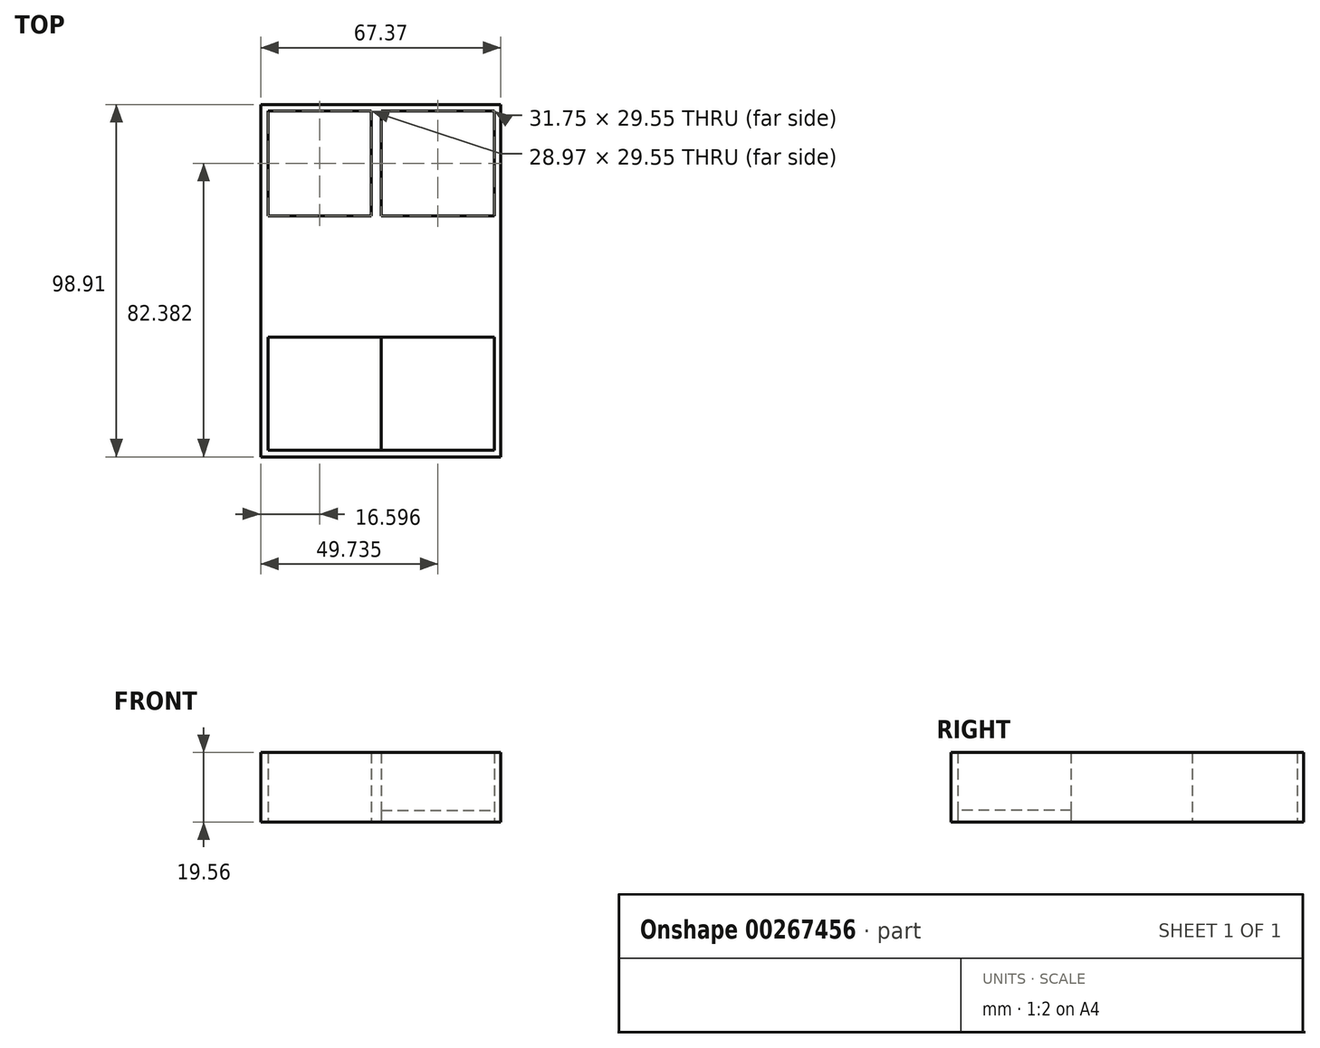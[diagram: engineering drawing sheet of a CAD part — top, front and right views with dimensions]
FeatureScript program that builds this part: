
annotation { "Feature Type Name" : "Feature", "Feature Type Description" : "" }
export const myFeature = defineFeature(function(context is Context, id is Id, definition is map)
    precondition{}
    {
        {
            var Q0;
            Q0=qCreatedBy(makeId("Top.planeOp"),FACE);
            var sketch = newSketch(context, id + "F0", { "sketchPlane" : qUnion([Q0])});
            skLineSegment(sketch, "E0.bottom", {"start": v(-31.75, 51.62) * mm, "end": v(31.75, 51.62) * mm});
            skLineSegment(sketch, "E0.top", {"start": v(-31.75, -43.63) * mm, "end": v(31.75, -43.63) * mm});
            skLineSegment(sketch, "E0.left", {"start": v(-31.75, 51.62) * mm, "end": v(-31.75, -43.63) * mm});
            skLineSegment(sketch, "E0.right", {"start": v(31.75, 51.62) * mm, "end": v(31.75, -43.63) * mm});
            skLineSegment(sketch, "E1.bottom", {"start": v(-31.75, 51.62) * mm, "end": v(0, 51.62) * mm});
            skLineSegment(sketch, "E1.top", {"start": v(-31.75, 19.87) * mm, "end": v(0, 19.87) * mm});
            skLineSegment(sketch, "E1.left", {"start": v(-31.75, 51.62) * mm, "end": v(-31.75, 19.87) * mm});
            skLineSegment(sketch, "E1.right", {"start": v(0, 51.62) * mm, "end": v(0, 19.87) * mm});
            skLineSegment(sketch, "E2.bottom", {"start": v(31.75, 51.62) * mm, "end": v(0, 51.62) * mm});
            skLineSegment(sketch, "E2.top", {"start": v(31.75, 19.87) * mm, "end": v(0, 19.87) * mm});
            skLineSegment(sketch, "E2.left", {"start": v(31.75, 51.62) * mm, "end": v(31.75, 19.87) * mm});
            skLineSegment(sketch, "E3.top", {"start": v(-31.75, -11.88) * mm, "end": v(0, -11.88) * mm});
            skLineSegment(sketch, "E3.left", {"start": v(-31.75, 19.87) * mm, "end": v(-31.75, -11.88) * mm});
            skLineSegment(sketch, "E3.right", {"start": v(0, 19.87) * mm, "end": v(0, -11.88) * mm});
            skLineSegment(sketch, "E4.bottom", {"start": v(0, 19.87) * mm, "end": v(31.75, 19.87) * mm});
            skLineSegment(sketch, "E4.top", {"start": v(0, -11.88) * mm, "end": v(31.75, -11.88) * mm});
            skLineSegment(sketch, "E4.right", {"start": v(31.75, 19.87) * mm, "end": v(31.75, -11.88) * mm});
            skLineSegment(sketch, "E5.bottom", {"start": v(-31.75, -43.63) * mm, "end": v(0, -43.63) * mm});
            skLineSegment(sketch, "E5.left", {"start": v(-31.75, -43.63) * mm, "end": v(-31.75, -11.88) * mm});
            skLineSegment(sketch, "E5.right", {"start": v(0, -43.63) * mm, "end": v(0, -11.88) * mm});
            skLineSegment(sketch, "E6.top", {"start": v(0, -43.63) * mm, "end": v(31.75, -43.63) * mm});
            skLineSegment(sketch, "E6.left", {"start": v(0, -11.88) * mm, "end": v(0, -43.63) * mm});
            skLineSegment(sketch, "E6.right", {"start": v(31.75, -11.88) * mm, "end": v(31.75, -43.63) * mm});
            skLineSegment(sketch, "E7.bottom", {"start": v(-33.86, 53.37) * mm, "end": v(33.51, 53.37) * mm});
            skLineSegment(sketch, "E7.top", {"start": v(-33.86, -45.54) * mm, "end": v(33.51, -45.54) * mm});
            skLineSegment(sketch, "E7.left", {"start": v(-33.86, 53.37) * mm, "end": v(-33.86, -45.54) * mm});
            skLineSegment(sketch, "E7.right", {"start": v(33.51, 53.37) * mm, "end": v(33.51, -45.54) * mm});
            skLineSegment(sketch, "E8", {"start": v(31.75, 22.06) * mm, "end": v(-31.75, 22.06) * mm});
            skLineSegment(sketch, "E9", {"start": v(31.75, -8.96) * mm, "end": v(-31.75, -8.96) * mm});
            skLineSegment(sketch, "E10", {"start": v(-2.78, -43.63) * mm, "end": v(-2.78, 51.62) * mm});
            skSolve(sketch);
        }
        {
            var Q0;
            Q0 = qSketchRegion(id + "F0", true);
            var Q1;
            {var subQ0=sQuery(id+"F0.wireOp",EDGE,"E1.right");var subQ5=sQuery(id+"F0.wireOp",EDGE,"E8");var subQ6=makeQuery(id+"F0.imprint","INTERSECT",VERTEX,{"derivedFrom":[subQ0,subQ5]});Q1=makeQuery(id+"F0.imprint","IMPRINT",FACE,{"disambiguationData":[TD([[makeQuery(id+"F0.imprint","IMPRINT",EDGE,{"disambiguationData":[TD([[subQ6,-1.0]])],"derivedFrom":subQ5}),-1.0]])]});}
            var Q2;
            {var subQ1=sQuery(id+"F0.wireOp",EDGE,"E1.right");var subQ3=sQuery(id+"F0.wireOp",EDGE,"E8");var subQ4=makeQuery(id+"F0.imprint","INTERSECT",VERTEX,{"derivedFrom":[subQ1,subQ3]});Q2=makeQuery(id+"F0.imprint","IMPRINT",FACE,{"disambiguationData":[TD([[makeQuery(id+"F0.imprint","IMPRINT",EDGE,{"disambiguationData":[TD([[subQ4,-1.0]])],"derivedFrom":subQ3}),1.0]])]});}
            var Q3;
            {var subQ0=sQuery(id+"F0.wireOp",EDGE,"E3.right");var subQ5=sQuery(id+"F0.wireOp",EDGE,"E9");var subQ6=makeQuery(id+"F0.imprint","INTERSECT",VERTEX,{"derivedFrom":[subQ0,subQ5]});Q3=makeQuery(id+"F0.imprint","IMPRINT",FACE,{"disambiguationData":[TD([[makeQuery(id+"F0.imprint","IMPRINT",EDGE,{"disambiguationData":[TD([[subQ6,-1.0]])],"derivedFrom":subQ5}),-1.0]])]});}
            var Q4;
            {var subQ1=sQuery(id+"F0.wireOp",EDGE,"E1.left");var subQ3=sQuery(id+"F0.wireOp",EDGE,"E8");var subQ4=makeQuery(id+"F0.imprint","INTERSECT",VERTEX,{"derivedFrom":[subQ1,subQ3]});Q4=makeQuery(id+"F0.imprint","IMPRINT",FACE,{"disambiguationData":[TD([[makeQuery(id+"F0.imprint","IMPRINT",EDGE,{"disambiguationData":[TD([[subQ4,1.0]])],"derivedFrom":subQ3}),1.0]])]});}
            var Q5;
            {var subQ0=sQuery(id+"F0.wireOp",EDGE,"E4.bottom");Q5=makeQuery(id+"F0.imprint","IMPRINT",FACE,{"disambiguationData":[TD([[makeQuery(id+"F0.imprint","IMPRINT",EDGE,{"derivedFrom":subQ0}),1.0]])]});}
            var Q6;
            {var subQ1=sQuery(id+"F0.wireOp",EDGE,"E3.left");var subQ3=sQuery(id+"F0.wireOp",EDGE,"E9");var subQ4=makeQuery(id+"F0.imprint","INTERSECT",VERTEX,{"derivedFrom":[subQ1,subQ3]});Q6=makeQuery(id+"F0.imprint","IMPRINT",FACE,{"disambiguationData":[TD([[makeQuery(id+"F0.imprint","IMPRINT",EDGE,{"disambiguationData":[TD([[subQ4,1.0]])],"derivedFrom":subQ3}),1.0]])]});}
            var Q7;
            {var subQ1=sQuery(id+"F0.wireOp",EDGE,"E3.right");var subQ3=sQuery(id+"F0.wireOp",EDGE,"E9");var subQ4=makeQuery(id+"F0.imprint","INTERSECT",VERTEX,{"derivedFrom":[subQ1,subQ3]});Q7=makeQuery(id+"F0.imprint","IMPRINT",FACE,{"disambiguationData":[TD([[makeQuery(id+"F0.imprint","IMPRINT",EDGE,{"disambiguationData":[TD([[subQ4,-1.0]])],"derivedFrom":subQ3}),1.0]])]});}
            var Q8;
            {var subQ0=sQuery(id+"F0.wireOp",EDGE,"E6.left");Q8=makeQuery(id+"F0.imprint","IMPRINT",FACE,{"disambiguationData":[TD([[makeQuery(id+"F0.imprint","IMPRINT",EDGE,{"derivedFrom":subQ0}),-1.0]])]});}
            var Q9;
            {var subQ0=sQuery(id+"F0.wireOp",EDGE,"E4.top");Q9=makeQuery(id+"F0.imprint","IMPRINT",FACE,{"disambiguationData":[TD([[makeQuery(id+"F0.imprint","IMPRINT",EDGE,{"derivedFrom":subQ0}),1.0]])]});}
            extrude(context, id + "F1", {"entities" : qUnion([Q0, Q1, Q2, Q3, Q4, Q5, Q6, Q7, Q8, Q9]), "depth" : 19.56 * mm});
        }
        {
            var Q0;
            Q0 = qSketchRegion(id + "F0", true);
            var Q1;
            {var subQ0=sQuery(id+"F0.wireOp",EDGE,"E2.bottom");Q1=makeQuery(id+"F0.imprint","IMPRINT",FACE,{"disambiguationData":[TD([[makeQuery(id+"F0.imprint","IMPRINT",EDGE,{"derivedFrom":subQ0}),1.0]])]});}
            var Q2;
            {var subQ0=sQuery(id+"F0.wireOp",EDGE,"E4.bottom");Q2=makeQuery(id+"F0.imprint","IMPRINT",FACE,{"disambiguationData":[TD([[makeQuery(id+"F0.imprint","IMPRINT",EDGE,{"derivedFrom":subQ0}),-1.0]])]});}
            var Q3;
            {var subQ0=sQuery(id+"F0.wireOp",EDGE,"E1.left");var subQ1=sQuery(id+"F0.wireOp",EDGE,"E1.bottom");var subQ2=makeQuery(id+"F0.imprint","INTERSECT",VERTEX,{"derivedFrom":[subQ1,subQ0]});Q3=makeQuery(id+"F0.imprint","IMPRINT",FACE,{"disambiguationData":[TD([[makeQuery(id+"F0.imprint","IMPRINT",EDGE,{"disambiguationData":[TD([[subQ2,-1.0]])],"derivedFrom":subQ1}),-1.0]])]});}
            var Q4;
            {var subQ0=sQuery(id+"F0.wireOp",EDGE,"E3.left");var subQ5=sQuery(id+"F0.wireOp",EDGE,"E9");var subQ6=makeQuery(id+"F0.imprint","INTERSECT",VERTEX,{"derivedFrom":[subQ0,subQ5]});Q4=makeQuery(id+"F0.imprint","IMPRINT",FACE,{"disambiguationData":[TD([[makeQuery(id+"F0.imprint","IMPRINT",EDGE,{"disambiguationData":[TD([[subQ6,1.0]])],"derivedFrom":subQ5}),-1.0]])]});}
            var Q5;
            {var subQ0=sQuery(id+"F0.wireOp",EDGE,"E5.left");Q5=makeQuery(id+"F0.imprint","IMPRINT",FACE,{"disambiguationData":[TD([[makeQuery(id+"F0.imprint","IMPRINT",EDGE,{"derivedFrom":subQ0}),-1.0]])]});}
            var Q6;
            Q6=makeQuery(id+"F0.imprint","IMPRINT",FACE,{"disambiguationData":[TD([[makeQuery(id+"F0.imprint","IMPRINT",EDGE,{"derivedFrom":sQuery(id+"F0.wireOp",EDGE,"E4.top")}),-1.0]])]});
            extrude(context, id + "F2", {"entities" : qUnion([Q0, Q1, Q2, Q3, Q4, Q5, Q6]), "operationType" : NewBodyOperationType.ADD, "depth" : 3.3 * mm});
        }
    });
